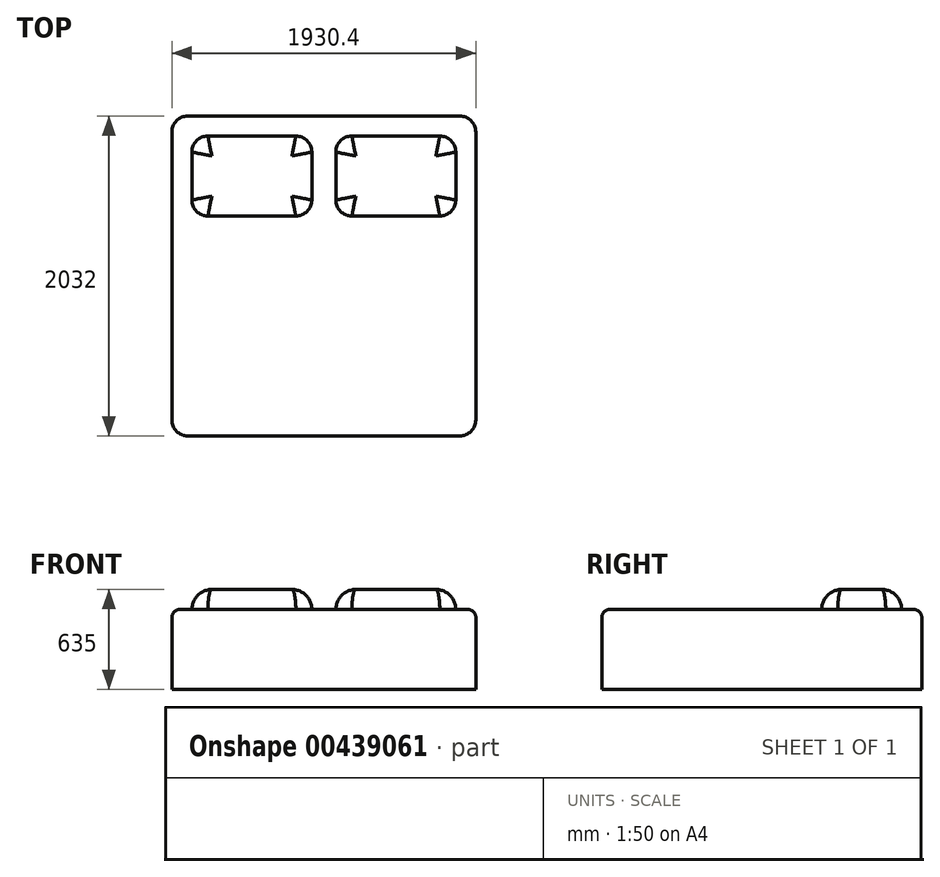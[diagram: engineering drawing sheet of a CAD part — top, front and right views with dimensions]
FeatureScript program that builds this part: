
annotation { "Feature Type Name" : "Feature", "Feature Type Description" : "" }
export const myFeature = defineFeature(function(context is Context, id is Id, definition is map)
    precondition{}
    {
        {
            var Q0;
            Q0=qCreatedBy(makeId("Top.planeOp"),FACE);
            var sketch = newSketch(context, id + "F0", { "sketchPlane" : qUnion([Q0])});
            skLineSegment(sketch, "E0.bottom", {"start": v(0, 0) * mm, "end": v(1930.4, 0) * mm});
            skLineSegment(sketch, "E0.top", {"start": v(0, 2032) * mm, "end": v(1930.4, 2032) * mm});
            skLineSegment(sketch, "E0.left", {"start": v(0, 0) * mm, "end": v(0, 2032) * mm});
            skLineSegment(sketch, "E0.right", {"start": v(1930.4, 0) * mm, "end": v(1930.4, 2032) * mm});
            skSolve(sketch);
        }
        {
            var Q0;
            Q0=qSketchRegion(id+"F0",true);
            extrude(context, id + "F1", {"entities" : qUnion([Q0]), "depth" : 508 * mm});
        }
        {
            var Q0;
            Q0=makeQuery(id+"F1.opExtrude","CAP_FACE",FACE,{"disambiguationData":[OSD([sQuery(id+"F0.wireOp",EDGE,"E0.bottom"),sQuery(id+"F0.wireOp",EDGE,"E0.top"),sQuery(id+"F0.wireOp",EDGE,"E0.left"),sQuery(id+"F0.wireOp",EDGE,"E0.right")])],"isStart":false});
            var sketch = newSketch(context, id + "F2", { "sketchPlane" : qUnion([Q0])});
            skLineSegment(sketch, "E1.bottom", {"start": v(127, 1905) * mm, "end": v(889, 1905) * mm});
            skLineSegment(sketch, "E1.top", {"start": v(127, 1397) * mm, "end": v(889, 1397) * mm});
            skLineSegment(sketch, "E1.left", {"start": v(127, 1905) * mm, "end": v(127, 1397) * mm});
            skLineSegment(sketch, "E1.right", {"start": v(889, 1905) * mm, "end": v(889, 1397) * mm});
            skLineSegment(sketch, "E2.bottom", {"start": v(1041.4, 1905) * mm, "end": v(1803.4, 1905) * mm});
            skLineSegment(sketch, "E2.top", {"start": v(1041.4, 1397) * mm, "end": v(1803.4, 1397) * mm});
            skLineSegment(sketch, "E2.left", {"start": v(1041.4, 1905) * mm, "end": v(1041.4, 1397) * mm});
            skLineSegment(sketch, "E2.right", {"start": v(1803.4, 1905) * mm, "end": v(1803.4, 1397) * mm});
            skSolve(sketch);
        }
        {
            var Q0;
            Q0=qSketchRegion(id+"F2",true);
            extrude(context, id + "F3", {"entities" : qUnion([Q0]), "operationType" : NewBodyOperationType.ADD, "depth" : 127 * mm});
        }
        {
            var Q0;
            Q0=makeQuery(id+"F1.opExtrude","SWEPT_EDGE",EDGE,{"disambiguationData":[OSD([sQuery(id+"F0.wireOp",EDGE,"E0.bottom"),sQuery(id+"F0.wireOp",EDGE,"E0.left")])]});
            var Q1;
            Q1=makeQuery(id+"F1.opExtrude","SWEPT_EDGE",EDGE,{"disambiguationData":[OSD([sQuery(id+"F0.wireOp",EDGE,"E0.bottom"),sQuery(id+"F0.wireOp",EDGE,"E0.right")])]});
            var Q2;
            Q2=makeQuery(id+"F1.opExtrude","SWEPT_EDGE",EDGE,{"disambiguationData":[OSD([sQuery(id+"F0.wireOp",EDGE,"E0.top"),sQuery(id+"F0.wireOp",EDGE,"E0.right")])]});
            var Q3;
            Q3=makeQuery(id+"F3.opExtrude","SWEPT_EDGE",EDGE,{"disambiguationData":[OSD([sQuery(id+"F2.wireOp",EDGE,"E2.bottom"),sQuery(id+"F2.wireOp",EDGE,"E2.right")])]});
            var Q4;
            Q4=makeQuery(id+"F3.opExtrude","SWEPT_EDGE",EDGE,{"disambiguationData":[OSD([sQuery(id+"F2.wireOp",EDGE,"E2.top"),sQuery(id+"F2.wireOp",EDGE,"E2.right")])]});
            var Q5;
            Q5=makeQuery(id+"F3.opExtrude","SWEPT_EDGE",EDGE,{"disambiguationData":[OSD([sQuery(id+"F2.wireOp",EDGE,"E2.top"),sQuery(id+"F2.wireOp",EDGE,"E2.left")])]});
            var Q6;
            Q6=makeQuery(id+"F3.opExtrude","SWEPT_EDGE",EDGE,{"disambiguationData":[OSD([sQuery(id+"F2.wireOp",EDGE,"E1.top"),sQuery(id+"F2.wireOp",EDGE,"E1.right")])]});
            var Q7;
            Q7=makeQuery(id+"F3.opExtrude","SWEPT_EDGE",EDGE,{"disambiguationData":[OSD([sQuery(id+"F2.wireOp",EDGE,"E1.bottom"),sQuery(id+"F2.wireOp",EDGE,"E1.right")])]});
            var Q8;
            Q8=makeQuery(id+"F3.opExtrude","SWEPT_EDGE",EDGE,{"disambiguationData":[OSD([sQuery(id+"F2.wireOp",EDGE,"E1.top"),sQuery(id+"F2.wireOp",EDGE,"E1.left")])]});
            var Q9;
            Q9=makeQuery(id+"F1.opExtrude","SWEPT_EDGE",EDGE,{"disambiguationData":[OSD([sQuery(id+"F0.wireOp",EDGE,"E0.top"),sQuery(id+"F0.wireOp",EDGE,"E0.left")])]});
            var Q10;
            Q10=makeQuery(id+"F3.opExtrude","SWEPT_EDGE",EDGE,{"disambiguationData":[OSD([sQuery(id+"F2.wireOp",EDGE,"E1.bottom"),sQuery(id+"F2.wireOp",EDGE,"E1.left")])]});
            var Q11;
            Q11=makeQuery(id+"F3.opExtrude","SWEPT_EDGE",EDGE,{"disambiguationData":[OSD([sQuery(id+"F2.wireOp",EDGE,"E2.bottom"),sQuery(id+"F2.wireOp",EDGE,"E2.left")])]});
            fillet(context, id + "F4", {"entities" : qUnion([Q0, Q1, Q2, Q3, Q4, Q5, Q6, Q7, Q8, Q9, Q10, Q11]), "radius" : 101.6 * mm, "tangentPropagation" : true, "allowEdgeOverflow" : false});
        }
        {
            var Q0;
            Q0=makeQuery(id+"F1.opExtrude","CAP_EDGE",EDGE,{"disambiguationData":[OSD([sQuery(id+"F0.wireOp",EDGE,"E0.left")])],"isStart":false});
            var Q1;
            {var subQ0=sQuery(id+"F0.wireOp",EDGE,"E0.left");var subQ1=sQuery(id+"F0.wireOp",EDGE,"E0.top");Q1=makeQuery(id+"F4.opFillet","BLEND_EDGE",EDGE,{"blendedFrom":[makeQuery(id+"F1.opExtrude","SWEPT_EDGE",EDGE,{"disambiguationData":[OSD([subQ1,subQ0])]}),makeQuery(id+"F1.opExtrude","CAP_FACE",FACE,{"disambiguationData":[OSD([sQuery(id+"F0.wireOp",EDGE,"E0.bottom"),subQ1,subQ0,sQuery(id+"F0.wireOp",EDGE,"E0.right")])],"isStart":false})],"blendedInto":[makeQuery(id+"F1.opExtrude","CAP_FACE",FACE,{"disambiguationData":[OSD([sQuery(id+"F0.wireOp",EDGE,"E0.bottom"),subQ1,subQ0,sQuery(id+"F0.wireOp",EDGE,"E0.right")])],"isStart":false})]});}
            var Q2;
            {var subQ0=sQuery(id+"F0.wireOp",EDGE,"E0.right");var subQ1=sQuery(id+"F0.wireOp",EDGE,"E0.top");Q2=makeQuery(id+"F4.opFillet","BLEND_EDGE",EDGE,{"blendedFrom":[makeQuery(id+"F1.opExtrude","SWEPT_EDGE",EDGE,{"disambiguationData":[OSD([subQ1,subQ0])]}),makeQuery(id+"F1.opExtrude","CAP_FACE",FACE,{"disambiguationData":[OSD([sQuery(id+"F0.wireOp",EDGE,"E0.bottom"),subQ1,sQuery(id+"F0.wireOp",EDGE,"E0.left"),subQ0])],"isStart":false})],"blendedInto":[makeQuery(id+"F1.opExtrude","CAP_FACE",FACE,{"disambiguationData":[OSD([sQuery(id+"F0.wireOp",EDGE,"E0.bottom"),subQ1,sQuery(id+"F0.wireOp",EDGE,"E0.left"),subQ0])],"isStart":false})]});}
            var Q3;
            Q3=makeQuery(id+"F1.opExtrude","CAP_EDGE",EDGE,{"disambiguationData":[OSD([sQuery(id+"F0.wireOp",EDGE,"E0.right")])],"isStart":false});
            var Q4;
            {var subQ0=sQuery(id+"F0.wireOp",EDGE,"E0.right");var subQ1=sQuery(id+"F0.wireOp",EDGE,"E0.bottom");Q4=makeQuery(id+"F4.opFillet","BLEND_EDGE",EDGE,{"blendedFrom":[makeQuery(id+"F1.opExtrude","SWEPT_EDGE",EDGE,{"disambiguationData":[OSD([subQ1,subQ0])]}),makeQuery(id+"F1.opExtrude","CAP_FACE",FACE,{"disambiguationData":[OSD([subQ1,sQuery(id+"F0.wireOp",EDGE,"E0.top"),sQuery(id+"F0.wireOp",EDGE,"E0.left"),subQ0])],"isStart":false})],"blendedInto":[makeQuery(id+"F1.opExtrude","CAP_FACE",FACE,{"disambiguationData":[OSD([subQ1,sQuery(id+"F0.wireOp",EDGE,"E0.top"),sQuery(id+"F0.wireOp",EDGE,"E0.left"),subQ0])],"isStart":false})]});}
            var Q5;
            Q5=makeQuery(id+"F1.opExtrude","CAP_EDGE",EDGE,{"disambiguationData":[OSD([sQuery(id+"F0.wireOp",EDGE,"E0.bottom")])],"isStart":false});
            var Q6;
            {var subQ0=sQuery(id+"F0.wireOp",EDGE,"E0.left");var subQ1=sQuery(id+"F0.wireOp",EDGE,"E0.bottom");Q6=makeQuery(id+"F4.opFillet","BLEND_EDGE",EDGE,{"blendedFrom":[makeQuery(id+"F1.opExtrude","SWEPT_EDGE",EDGE,{"disambiguationData":[OSD([subQ1,subQ0])]}),makeQuery(id+"F1.opExtrude","CAP_FACE",FACE,{"disambiguationData":[OSD([subQ1,sQuery(id+"F0.wireOp",EDGE,"E0.top"),subQ0,sQuery(id+"F0.wireOp",EDGE,"E0.right")])],"isStart":false})],"blendedInto":[makeQuery(id+"F1.opExtrude","CAP_FACE",FACE,{"disambiguationData":[OSD([subQ1,sQuery(id+"F0.wireOp",EDGE,"E0.top"),subQ0,sQuery(id+"F0.wireOp",EDGE,"E0.right")])],"isStart":false})]});}
            var Q7;
            Q7=makeQuery(id+"F1.opExtrude","CAP_EDGE",EDGE,{"disambiguationData":[OSD([sQuery(id+"F0.wireOp",EDGE,"E0.top")])],"isStart":false});
            fillet(context, id + "F5", {"entities" : qUnion([Q0, Q1, Q2, Q3, Q4, Q5, Q6, Q7]), "radius" : 50.8 * mm, "tangentPropagation" : true, "allowEdgeOverflow" : false});
        }
        {
            var Q0;
            {var subQ0=sQuery(id+"F2.wireOp",EDGE,"E1.left");var subQ1=sQuery(id+"F2.wireOp",EDGE,"E1.top");Q0=makeQuery(id+"F4.opFillet","BLEND_EDGE",EDGE,{"blendedFrom":[makeQuery(id+"F3.opExtrude","SWEPT_EDGE",EDGE,{"disambiguationData":[OSD([subQ1,subQ0])]}),makeQuery(id+"F3.opExtrude","CAP_FACE",FACE,{"disambiguationData":[OSD([sQuery(id+"F2.wireOp",EDGE,"E1.bottom"),subQ1,subQ0,sQuery(id+"F2.wireOp",EDGE,"E1.right")])],"isStart":false})],"blendedInto":[makeQuery(id+"F3.opExtrude","CAP_FACE",FACE,{"disambiguationData":[OSD([sQuery(id+"F2.wireOp",EDGE,"E1.bottom"),subQ1,subQ0,sQuery(id+"F2.wireOp",EDGE,"E1.right")])],"isStart":false})]});}
            var Q1;
            Q1=makeQuery(id+"F3.opExtrude","CAP_EDGE",EDGE,{"disambiguationData":[OSD([sQuery(id+"F2.wireOp",EDGE,"E1.left")])],"isStart":false});
            var Q2;
            {var subQ0=sQuery(id+"F2.wireOp",EDGE,"E1.left");var subQ1=sQuery(id+"F2.wireOp",EDGE,"E1.bottom");Q2=makeQuery(id+"F4.opFillet","BLEND_EDGE",EDGE,{"blendedFrom":[makeQuery(id+"F3.opExtrude","SWEPT_EDGE",EDGE,{"disambiguationData":[OSD([subQ1,subQ0])]}),makeQuery(id+"F3.opExtrude","CAP_FACE",FACE,{"disambiguationData":[OSD([subQ1,sQuery(id+"F2.wireOp",EDGE,"E1.top"),subQ0,sQuery(id+"F2.wireOp",EDGE,"E1.right")])],"isStart":false})],"blendedInto":[makeQuery(id+"F3.opExtrude","CAP_FACE",FACE,{"disambiguationData":[OSD([subQ1,sQuery(id+"F2.wireOp",EDGE,"E1.top"),subQ0,sQuery(id+"F2.wireOp",EDGE,"E1.right")])],"isStart":false})]});}
            var Q3;
            Q3=makeQuery(id+"F3.opExtrude","CAP_EDGE",EDGE,{"disambiguationData":[OSD([sQuery(id+"F2.wireOp",EDGE,"E1.bottom")])],"isStart":false});
            var Q4;
            {var subQ0=sQuery(id+"F2.wireOp",EDGE,"E1.right");var subQ1=sQuery(id+"F2.wireOp",EDGE,"E1.bottom");Q4=makeQuery(id+"F4.opFillet","BLEND_EDGE",EDGE,{"blendedFrom":[makeQuery(id+"F3.opExtrude","SWEPT_EDGE",EDGE,{"disambiguationData":[OSD([subQ1,subQ0])]}),makeQuery(id+"F3.opExtrude","CAP_FACE",FACE,{"disambiguationData":[OSD([subQ1,sQuery(id+"F2.wireOp",EDGE,"E1.top"),sQuery(id+"F2.wireOp",EDGE,"E1.left"),subQ0])],"isStart":false})],"blendedInto":[makeQuery(id+"F3.opExtrude","CAP_FACE",FACE,{"disambiguationData":[OSD([subQ1,sQuery(id+"F2.wireOp",EDGE,"E1.top"),sQuery(id+"F2.wireOp",EDGE,"E1.left"),subQ0])],"isStart":false})]});}
            var Q5;
            {var subQ0=sQuery(id+"F2.wireOp",EDGE,"E1.right");var subQ1=sQuery(id+"F2.wireOp",EDGE,"E1.top");Q5=makeQuery(id+"F4.opFillet","BLEND_EDGE",EDGE,{"blendedFrom":[makeQuery(id+"F3.opExtrude","SWEPT_EDGE",EDGE,{"disambiguationData":[OSD([subQ1,subQ0])]}),makeQuery(id+"F3.opExtrude","CAP_FACE",FACE,{"disambiguationData":[OSD([sQuery(id+"F2.wireOp",EDGE,"E1.bottom"),subQ1,sQuery(id+"F2.wireOp",EDGE,"E1.left"),subQ0])],"isStart":false})],"blendedInto":[makeQuery(id+"F3.opExtrude","CAP_FACE",FACE,{"disambiguationData":[OSD([sQuery(id+"F2.wireOp",EDGE,"E1.bottom"),subQ1,sQuery(id+"F2.wireOp",EDGE,"E1.left"),subQ0])],"isStart":false})]});}
            var Q6;
            Q6=makeQuery(id+"F3.opExtrude","CAP_EDGE",EDGE,{"disambiguationData":[OSD([sQuery(id+"F2.wireOp",EDGE,"E1.right")])],"isStart":false});
            var Q7;
            Q7=makeQuery(id+"F3.opExtrude","CAP_EDGE",EDGE,{"disambiguationData":[OSD([sQuery(id+"F2.wireOp",EDGE,"E1.top")])],"isStart":false});
            var Q8;
            {var subQ0=sQuery(id+"F2.wireOp",EDGE,"E2.left");var subQ1=sQuery(id+"F2.wireOp",EDGE,"E2.bottom");Q8=makeQuery(id+"F4.opFillet","BLEND_EDGE",EDGE,{"blendedFrom":[makeQuery(id+"F3.opExtrude","SWEPT_EDGE",EDGE,{"disambiguationData":[OSD([subQ1,subQ0])]}),makeQuery(id+"F3.opExtrude","CAP_FACE",FACE,{"disambiguationData":[OSD([subQ1,sQuery(id+"F2.wireOp",EDGE,"E2.top"),subQ0,sQuery(id+"F2.wireOp",EDGE,"E2.right")])],"isStart":false})],"blendedInto":[makeQuery(id+"F3.opExtrude","CAP_FACE",FACE,{"disambiguationData":[OSD([subQ1,sQuery(id+"F2.wireOp",EDGE,"E2.top"),subQ0,sQuery(id+"F2.wireOp",EDGE,"E2.right")])],"isStart":false})]});}
            var Q9;
            Q9=makeQuery(id+"F3.opExtrude","CAP_EDGE",EDGE,{"disambiguationData":[OSD([sQuery(id+"F2.wireOp",EDGE,"E2.left")])],"isStart":false});
            var Q10;
            {var subQ0=sQuery(id+"F2.wireOp",EDGE,"E2.left");var subQ1=sQuery(id+"F2.wireOp",EDGE,"E2.top");Q10=makeQuery(id+"F4.opFillet","BLEND_EDGE",EDGE,{"blendedFrom":[makeQuery(id+"F3.opExtrude","SWEPT_EDGE",EDGE,{"disambiguationData":[OSD([subQ1,subQ0])]}),makeQuery(id+"F3.opExtrude","CAP_FACE",FACE,{"disambiguationData":[OSD([sQuery(id+"F2.wireOp",EDGE,"E2.bottom"),subQ1,subQ0,sQuery(id+"F2.wireOp",EDGE,"E2.right")])],"isStart":false})],"blendedInto":[makeQuery(id+"F3.opExtrude","CAP_FACE",FACE,{"disambiguationData":[OSD([sQuery(id+"F2.wireOp",EDGE,"E2.bottom"),subQ1,subQ0,sQuery(id+"F2.wireOp",EDGE,"E2.right")])],"isStart":false})]});}
            var Q11;
            Q11=makeQuery(id+"F3.opExtrude","CAP_EDGE",EDGE,{"disambiguationData":[OSD([sQuery(id+"F2.wireOp",EDGE,"E2.top")])],"isStart":false});
            var Q12;
            Q12=makeQuery(id+"F3.opExtrude","CAP_EDGE",EDGE,{"disambiguationData":[OSD([sQuery(id+"F2.wireOp",EDGE,"E2.right")])],"isStart":false});
            var Q13;
            {var subQ0=sQuery(id+"F2.wireOp",EDGE,"E2.right");var subQ1=sQuery(id+"F2.wireOp",EDGE,"E2.top");Q13=makeQuery(id+"F4.opFillet","BLEND_EDGE",EDGE,{"blendedFrom":[makeQuery(id+"F3.opExtrude","SWEPT_EDGE",EDGE,{"disambiguationData":[OSD([subQ1,subQ0])]}),makeQuery(id+"F3.opExtrude","CAP_FACE",FACE,{"disambiguationData":[OSD([sQuery(id+"F2.wireOp",EDGE,"E2.bottom"),subQ1,sQuery(id+"F2.wireOp",EDGE,"E2.left"),subQ0])],"isStart":false})],"blendedInto":[makeQuery(id+"F3.opExtrude","CAP_FACE",FACE,{"disambiguationData":[OSD([sQuery(id+"F2.wireOp",EDGE,"E2.bottom"),subQ1,sQuery(id+"F2.wireOp",EDGE,"E2.left"),subQ0])],"isStart":false})]});}
            var Q14;
            {var subQ0=sQuery(id+"F2.wireOp",EDGE,"E2.right");var subQ1=sQuery(id+"F2.wireOp",EDGE,"E2.bottom");Q14=makeQuery(id+"F4.opFillet","BLEND_EDGE",EDGE,{"blendedFrom":[makeQuery(id+"F3.opExtrude","SWEPT_EDGE",EDGE,{"disambiguationData":[OSD([subQ1,subQ0])]}),makeQuery(id+"F3.opExtrude","CAP_FACE",FACE,{"disambiguationData":[OSD([subQ1,sQuery(id+"F2.wireOp",EDGE,"E2.top"),sQuery(id+"F2.wireOp",EDGE,"E2.left"),subQ0])],"isStart":false})],"blendedInto":[makeQuery(id+"F3.opExtrude","CAP_FACE",FACE,{"disambiguationData":[OSD([subQ1,sQuery(id+"F2.wireOp",EDGE,"E2.top"),sQuery(id+"F2.wireOp",EDGE,"E2.left"),subQ0])],"isStart":false})]});}
            var Q15;
            Q15=makeQuery(id+"F3.opExtrude","CAP_EDGE",EDGE,{"disambiguationData":[OSD([sQuery(id+"F2.wireOp",EDGE,"E2.bottom")])],"isStart":false});
            fillet(context, id + "F6", {"entities" : qUnion([Q0, Q1, Q2, Q3, Q4, Q5, Q6, Q7, Q8, Q9, Q10, Q11, Q12, Q13, Q14, Q15]), "radius" : 127 * mm, "tangentPropagation" : true, "allowEdgeOverflow" : false});
        }
    });
